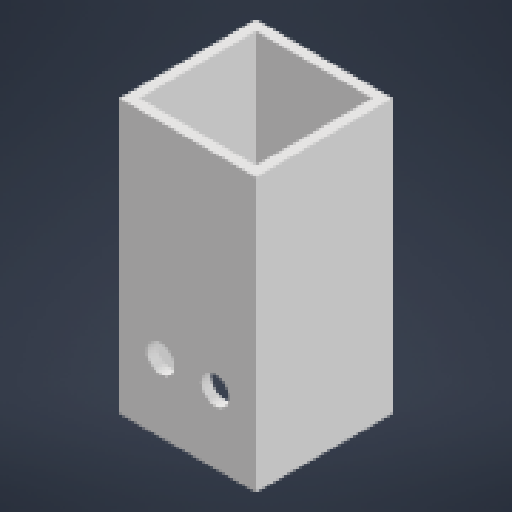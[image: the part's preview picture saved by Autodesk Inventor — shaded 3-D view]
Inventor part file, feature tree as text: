
AUTODESK INVENTOR PART (.ipt)
format: ipt  version: 2024 (Build 280153000, 153)  size: 148,992 bytes
history: native  units: mm
features: extrude x2, sketch x2, other x1
ambient origin geometry x8: Origin, YZ Plane, XZ Plane, XY Plane, X Axis, Y Axis, Z Axis, Center Point
bodies: Body1 (feature_tree)
feature tree (5):
  other  "Твердое тело1"
  extrude  "Выдавливание1"  Depth=20.0mm
  extrude  "Выдавливание2"  Depth=1.5mm
  sketch  "Эскиз1"
  sketch  "Эскиз2"
